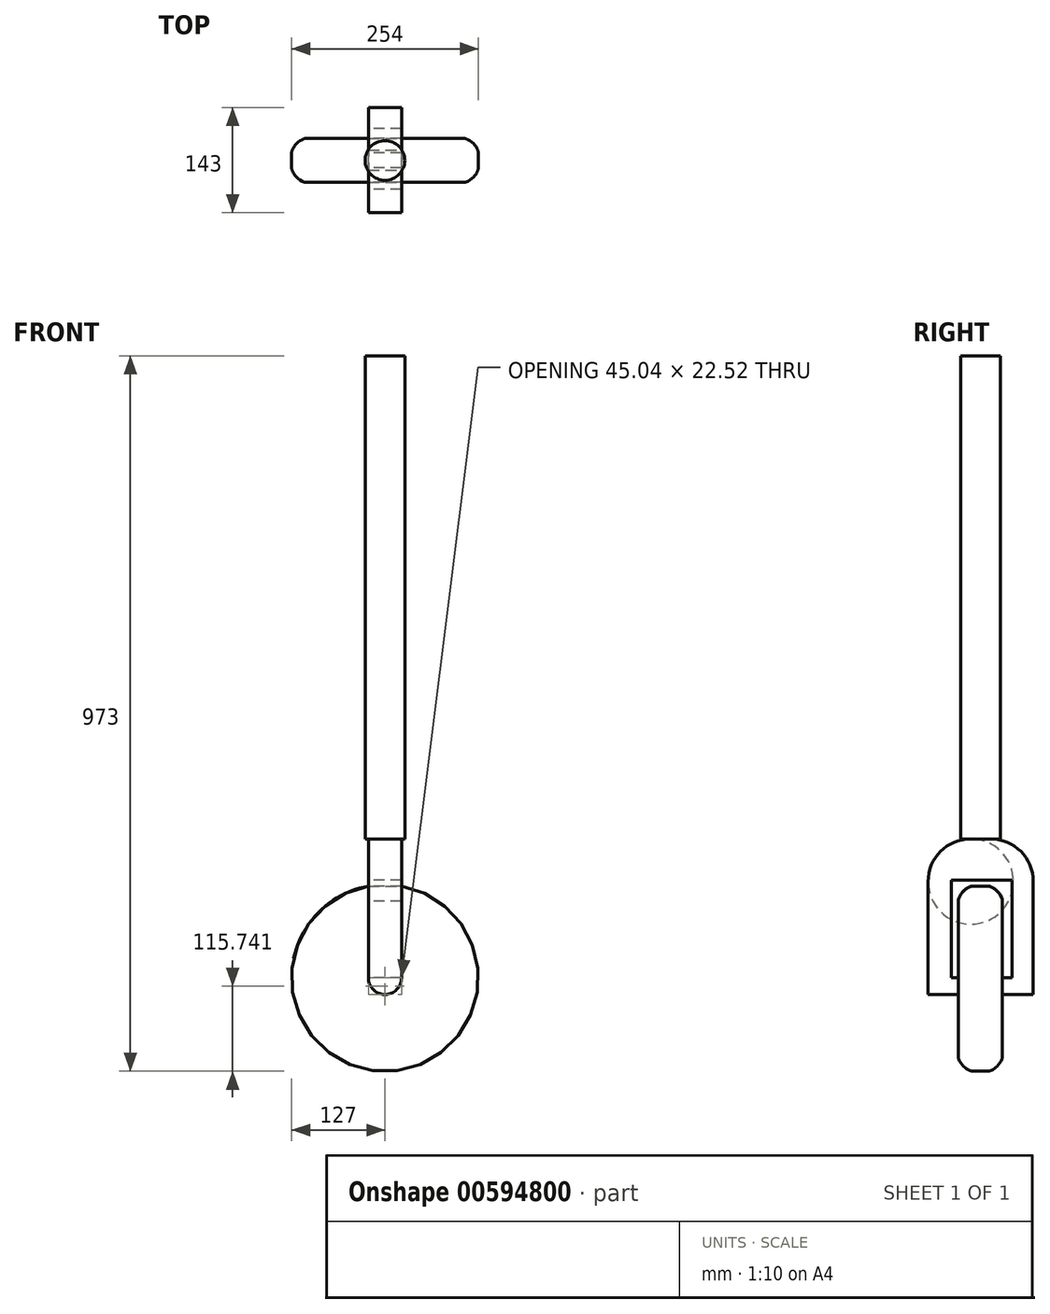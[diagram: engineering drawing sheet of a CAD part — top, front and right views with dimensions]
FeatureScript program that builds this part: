
annotation { "Feature Type Name" : "Feature", "Feature Type Description" : "" }
export const myFeature = defineFeature(function(context is Context, id is Id, definition is map)
    precondition{}
    {
        {
            var Q0;
            Q0=qCreatedBy(makeId("Front.planeOp"),FACE);
            var sketch = newSketch(context, id + "F0", { "sketchPlane" : qUnion([Q0])});
            skCircle(sketch, "E0", {"center": v(0, 0) * mm, "radius": 127 * mm});
            skCircle(sketch, "E1", {"center": v(0, 0) * mm, "radius": 25 * mm});
            skCircle(sketch, "E2", {"center": v(0, 0) * mm, "radius": 15 * mm});
            skCircle(sketch, "E3", {"center": v(0, 0) * mm, "radius": 14.5 * mm});
            skSolve(sketch);
        }
        {
            var Q0;
            Q0=makeQuery(id+"F0.imprint","IMPRINT",FACE,{"disambiguationData":[TD([[makeQuery(id+"F0.imprint","IMPRINT",EDGE,{"derivedFrom":sQuery(id+"F0.wireOp",EDGE,"E0")}),1.0]])]});
            var Q1;
            Q1=makeQuery(id+"F0.imprint","IMPRINT",FACE,{"disambiguationData":[TD([[makeQuery(id+"F0.imprint","IMPRINT",EDGE,{"derivedFrom":sQuery(id+"F0.wireOp",EDGE,"E1")}),1.0]])]});
            extrude(context, id + "F1", {"entities" : qUnion([Q0, Q1]), "endBound" : BoundingType.SYMMETRIC, "depth" : 60 * mm, "offsetDistance" : 25 * mm});
        }
        {
            var Q0;
            Q0=makeQuery(id+"F1.opExtrude","CAP_EDGE",EDGE,{"disambiguationData":[OSD([sQuery(id+"F0.wireOp",EDGE,"E0")])],"isStart":false});
            var Q1;
            Q1=makeQuery(id+"F1.opExtrude","CAP_EDGE",EDGE,{"disambiguationData":[OSD([sQuery(id+"F0.wireOp",EDGE,"E0")])],"isStart":true});
            fillet(context, id + "F2", {"entities" : qUnion([Q0, Q1]), "radius" : 20 * mm, "tangentPropagation" : true, "rho" : .3, "crossSection" : FilletCrossSection.CONIC, "allowEdgeOverflow" : false});
        }
        {
            var Q0;
            Q0=makeQuery(id+"F1.opExtrude","CAP_FACE",FACE,{"disambiguationData":[OSD([sQuery(id+"F0.wireOp",EDGE,"E0"),sQuery(id+"F0.wireOp",EDGE,"E2")])],"isStart":true});
            var sketch = newSketch(context, id + "F3", { "sketchPlane" : qUnion([Q0])});
            skCircle(sketch, "E4", {"center": v(0, 0) * mm, "radius": 22.52 * mm});
            skSolve(sketch);
        }
        {
            var Q0;
            Q0 = qSketchRegion(id + "F3", true);
            extrude(context, id + "F4", {"entities" : qUnion([Q0]), "operationType" : NewBodyOperationType.ADD, "oppositeDirection" : true, "depth" : 101 * mm, "offsetDistance" : 25 * mm, "hasSecondDirection" : true, "secondDirectionOppositeDirection" : false, "secondDirectionDepth" : 42 * mm});
        }
        {
            var Q0;
            Q0=qCreatedBy(makeId("Top.planeOp"),FACE);
            var sketch = newSketch(context, id + "F5", { "sketchPlane" : qUnion([Q0])});
            skLineSegment(sketch, "E5", {"start": v(22.52, 72) * mm, "end": v(22.52, 30) * mm});
            skLineSegment(sketch, "E6", {"start": v(-22.52, 30) * mm, "end": v(-22.52, 72) * mm});
            skLineSegment(sketch, "E7", {"start": v(22.52, -30) * mm, "end": v(22.52, -71) * mm});
            skLineSegment(sketch, "E8", {"start": v(-22.52, -71) * mm, "end": v(-22.52, -30) * mm});
            skLineSegment(sketch, "E9.bottom", {"start": v(-22.52, 72) * mm, "end": v(22.52, 72) * mm});
            skLineSegment(sketch, "E9.top", {"start": v(-22.52, -71) * mm, "end": v(22.52, -71) * mm});
            skLineSegment(sketch, "E9.left", {"start": v(-22.52, 72) * mm, "end": v(-22.52, -71) * mm});
            skLineSegment(sketch, "E9.right", {"start": v(22.52, 72) * mm, "end": v(22.52, -71) * mm});
            skSolve(sketch);
        }
        {
            var Q0;
            Q0 = qSketchRegion(id + "F5", true);
            var Q1;
            Q1 = qConstructionFilter(qBodyType(qCreatedBy(id + "F5" ,EDGE), BodyType.WIRE), ConstructionObject.NO);
            extrude(context, id + "F6", {"entities" : qUnion([Q0]), "operationType" : NewBodyOperationType.ADD, "surfaceEntities" : qUnion([Q1]), "depth" : 189 * mm, "offsetDistance" : 25 * mm});
        }
        {
            var Q0;
            Q0=makeQuery(id+"F6.opExtrude","SWEPT_FACE",FACE,{"disambiguationData":[OSD([sQuery(id+"F5.wireOp",EDGE,"E9.left")])]});
            var sketch = newSketch(context, id + "F7", { "sketchPlane" : qUnion([Q0])});
            skLineSegment(sketch, "E10", {"start": v(-43.13, 0) * mm, "end": v(-43.13, 133.05) * mm});
            skLineSegment(sketch, "E11", {"start": v(-43.13, 133.05) * mm, "end": v(39.4, 133.05) * mm});
            skLineSegment(sketch, "E12", {"start": v(39.4, 133.05) * mm, "end": v(39.4, 0) * mm});
            skPoint(sketch, "E12.endSnap0", {"position": v(50.5, 0) * mm});
            skLineSegment(sketch, "E13.0", {"start": v(-72, 0) * mm, "end": v(-30, 0) * mm});
            skFitSpline(sketch, "E14.0", {"points": [v(-30, 104.6) * mm, v(-30, 34.06) * mm, v(-30, -36.47) * mm, v(-30, -107) * mm]});
            skPoint(sketch, "E15.0", {"position": v(-23.06, 117.8) * mm});
            skPoint(sketch, "E16.0", {"position": v(0, 124.99) * mm});
            skFitSpline(sketch, "E17.0", {"points": [v(-10, 124.98) * mm, v(-10.65, 124.98) * mm, v(-11.6, 124.86) * mm, v(-12.82, 124.54) * mm, v(-13.73, 124.23) * mm, v(-14.62, 123.87) * mm, v(-15.77, 123.34) * mm, v(-17.16, 122.57) * mm, v(-18.75, 121.52) * mm, v(-20.78, 119.98) * mm, v(-23.11, 117.85) * mm, v(-25.18, 115.48) * mm, v(-26.49, 113.68) * mm, v(-27.18, 112.6) * mm, v(-27.84, 111.52) * mm, v(-28.43, 110.4) * mm, v(-28.95, 109.23) * mm, v(-29.3, 108.33) * mm, v(-29.58, 107.42) * mm, v(-29.88, 106.19) * mm, v(-30, 105.24) * mm, v(-30, 104.6) * mm]});
            skLineSegment(sketch, "E18.0", {"start": v(-10, 124.99) * mm, "end": v(10, 124.99) * mm});
            skFitSpline(sketch, "E19.0", {"points": [v(30, 104.6) * mm, v(30, 105.24) * mm, v(29.88, 106.19) * mm, v(29.58, 107.42) * mm, v(29.29, 108.34) * mm, v(28.95, 109.23) * mm, v(28.43, 110.4) * mm, v(27.7, 111.8) * mm, v(26.68, 113.4) * mm, v(25.56, 114.96) * mm, v(24.35, 116.43) * mm, v(22.64, 118.28) * mm, v(20.78, 119.98) * mm, v(18.76, 121.51) * mm, v(17.16, 122.57) * mm, v(15.77, 123.34) * mm, v(14.62, 123.87) * mm, v(13.73, 124.23) * mm, v(12.82, 124.54) * mm, v(11.6, 124.86) * mm, v(10.65, 124.98) * mm, v(10, 124.98) * mm]});
            skFitSpline(sketch, "E20.0", {"points": [v(30, 104.6) * mm, v(30, 34.06) * mm, v(30, -36.47) * mm, v(30, -107) * mm]});
            skPoint(sketch, "E21.0", {"position": v(30, 0) * mm});
            skLineSegment(sketch, "E22.0", {"start": v(30, 0) * mm, "end": v(71, 0) * mm});
            skSolve(sketch);
        }
        {
            var Q0;
            {var subQ3=sQuery(id+"F7.wireOp",EDGE,"E10");Q0=makeQuery(id+"F7.imprint","IMPRINT",FACE,{"disambiguationData":[TD([[makeQuery(id+"F7.imprint","IMPRINT",EDGE,{"derivedFrom":subQ3}),-1.0]])]});}
            extrude(context, id + "F8", {"entities" : qUnion([Q0]), "operationType" : NewBodyOperationType.REMOVE, "endBound" : BoundingType.THROUGH_ALL, "oppositeDirection" : true, "depth" : 25 * mm, "offsetDistance" : 25 * mm});
        }
        {
            var Q0;
            Q0=makeQuery(id+"F6.opExtrude","CAP_EDGE",EDGE,{"disambiguationData":[OSD([sQuery(id+"F5.wireOp",EDGE,"E9.bottom")])],"isStart":false});
            var Q1;
            Q1=makeQuery(id+"F6.opExtrude","CAP_EDGE",EDGE,{"disambiguationData":[OSD([sQuery(id+"F5.wireOp",EDGE,"E9.top")])],"isStart":false});
            fillet(context, id + "F9", {"entities" : qUnion([Q0, Q1]), "radius" : 57.94 * mm, "tangentPropagation" : true, "allowEdgeOverflow" : false});
        }
        {
            var Q0;
            Q0=makeQuery(id+"F6.opExtrude","CAP_FACE",FACE,{"disambiguationData":[OSD([sQuery(id+"F5.wireOp",EDGE,"E9.bottom"),sQuery(id+"F5.wireOp",EDGE,"E9.top"),sQuery(id+"F5.wireOp",EDGE,"E9.left"),sQuery(id+"F5.wireOp",EDGE,"E9.right")])],"isStart":false});
            var sketch = newSketch(context, id + "F10", { "sketchPlane" : qUnion([Q0])});
            skCircle(sketch, "E23", {"center": v(0, 0) * mm, "radius": 27 * mm});
            skSolve(sketch);
        }
        {
            var Q0;
            Q0 = qSketchRegion(id + "F10", true);
            extrude(context, id + "F11", {"entities" : qUnion([Q0]), "operationType" : NewBodyOperationType.ADD, "depth" : 657 * mm, "offsetDistance" : 25 * mm});
        }
    });
